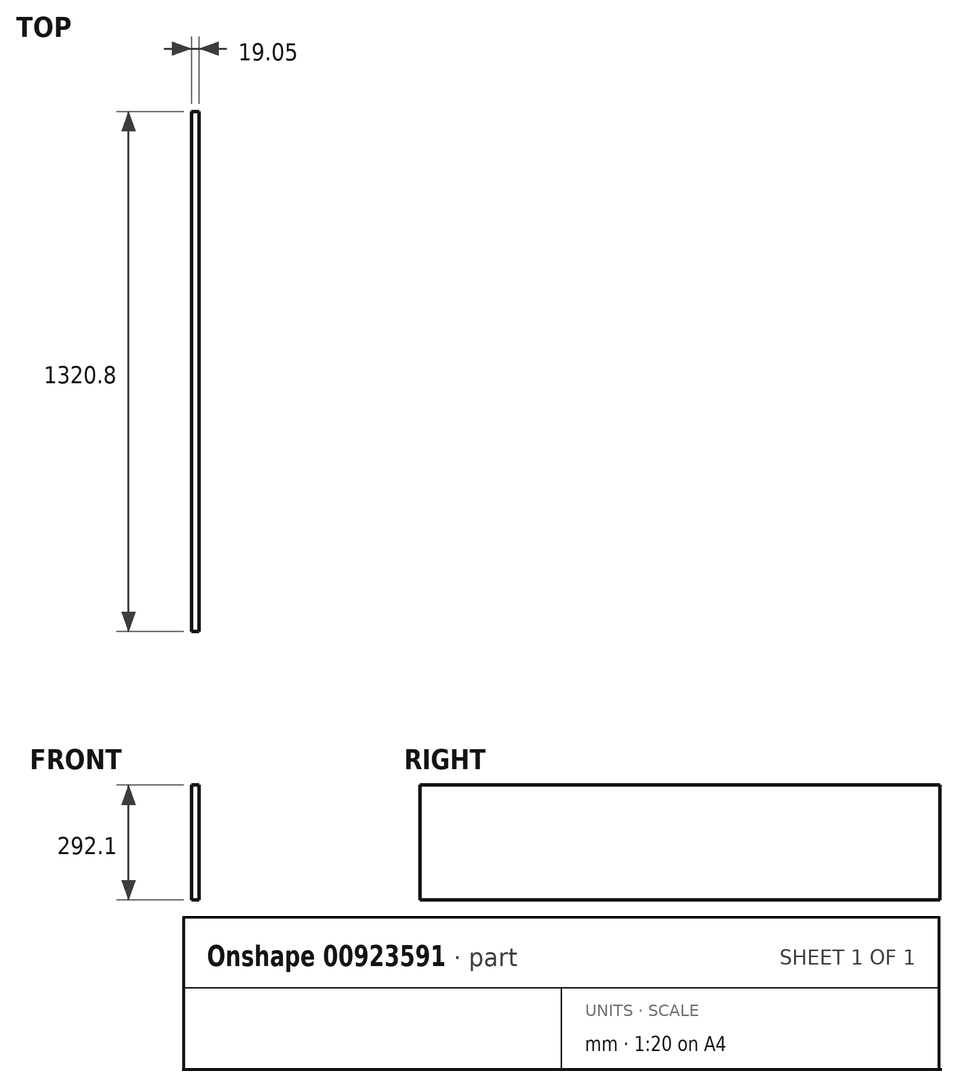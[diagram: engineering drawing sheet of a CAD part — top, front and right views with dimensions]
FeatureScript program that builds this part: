
annotation { "Feature Type Name" : "Feature", "Feature Type Description" : "" }
export const myFeature = defineFeature(function(context is Context, id is Id, definition is map)
    precondition{}
    {
        {
            var Q0;
            Q0=qCreatedBy(makeId("Right.planeOp"),FACE);
            var sketch = newSketch(context, id + "F0", { "sketchPlane" : qUnion([Q0])});
            skLineSegment(sketch, "E0.bottom", {"start": v(0, 0) * mm, "end": v(1320.8, 0) * mm});
            skLineSegment(sketch, "E0.top", {"start": v(0, 292.1) * mm, "end": v(1320.8, 292.1) * mm});
            skLineSegment(sketch, "E0.left", {"start": v(0, 0) * mm, "end": v(0, 292.1) * mm});
            skLineSegment(sketch, "E0.right", {"start": v(1320.8, 0) * mm, "end": v(1320.8, 292.1) * mm});
            skSolve(sketch);
        }
        {
            var Q0;
            Q0 = qSketchRegion(id + "F0", true);
            extrude(context, id + "F1", {"entities" : qUnion([Q0]), "depth" : 19.05 * mm, "offsetDistance" : 25.4 * mm});
        }
    });
